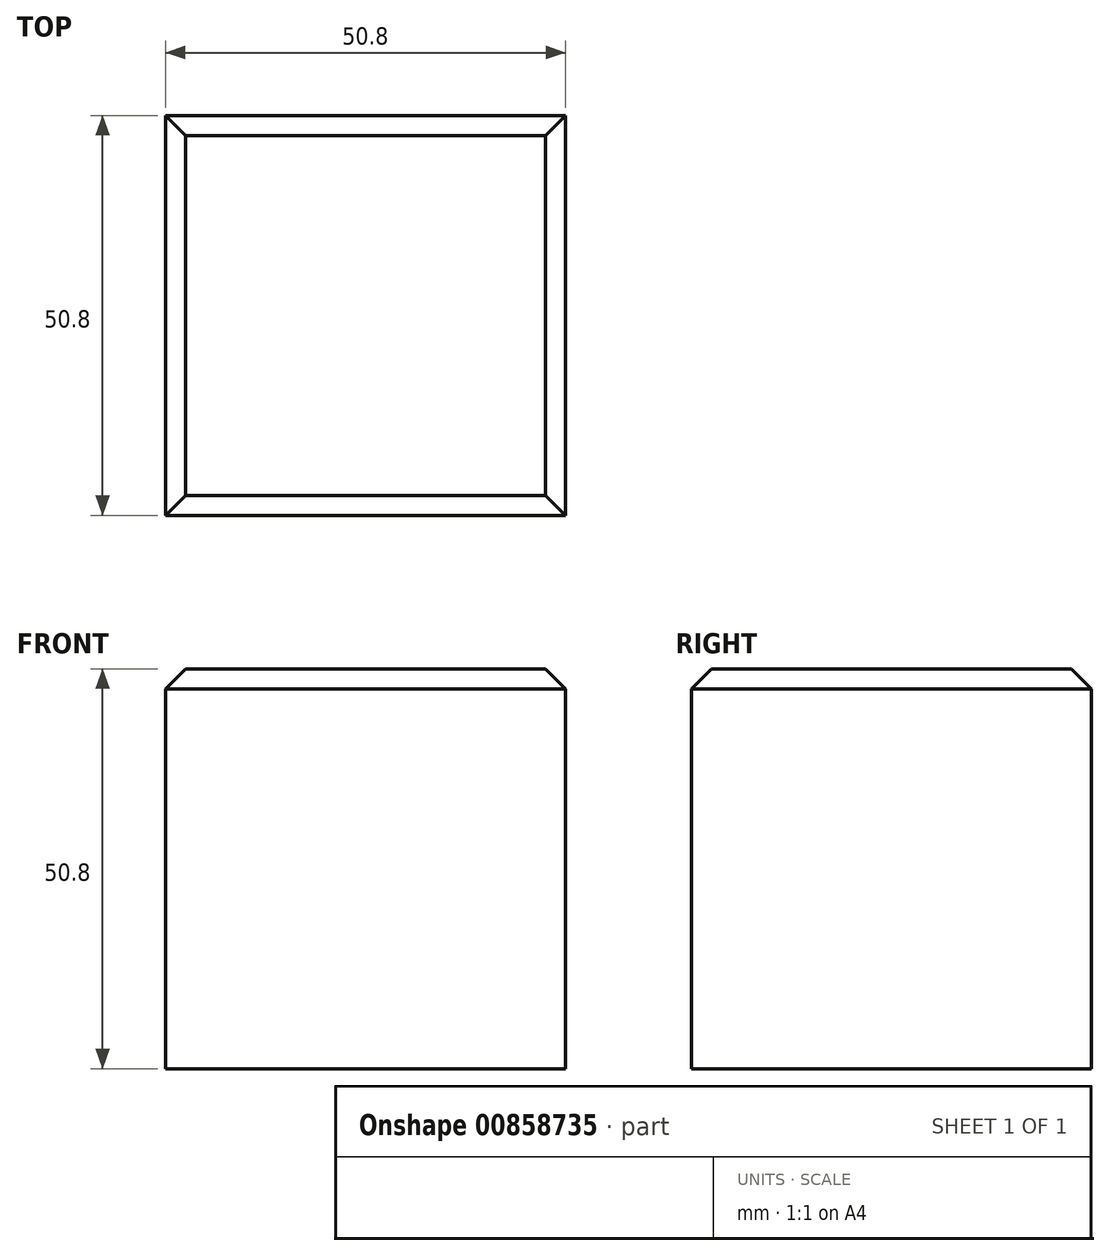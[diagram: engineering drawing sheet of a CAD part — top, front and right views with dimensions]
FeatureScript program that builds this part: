
annotation { "Feature Type Name" : "Feature", "Feature Type Description" : "" }
export const myFeature = defineFeature(function(context is Context, id is Id, definition is map)
    precondition{}
    {
        {
            var Q0;
            Q0=qCreatedBy(makeId("Top.planeOp"),FACE);
            var sketch = newSketch(context, id + "F0", { "sketchPlane" : qUnion([Q0])});
            skLineSegment(sketch, "E0.bottom", {"start": v(-25.4, 25.4) * mm, "end": v(25.4, 25.4) * mm});
            skLineSegment(sketch, "E0.top", {"start": v(-25.4, -25.4) * mm, "end": v(25.4, -25.4) * mm});
            skLineSegment(sketch, "E0.left", {"start": v(-25.4, 25.4) * mm, "end": v(-25.4, -25.4) * mm});
            skLineSegment(sketch, "E0.right", {"start": v(25.4, 25.4) * mm, "end": v(25.4, -25.4) * mm});
            skPoint(sketch, "E0.middle", {"position": v(0, 0) * mm});
            skSolve(sketch);
        }
        {
            var Q0;
            Q0 = qSketchRegion(id + "F0", true);
            extrude(context, id + "F1", {"entities" : qUnion([Q0]), "endBound" : BoundingType.SYMMETRIC, "depth" : 50.8 * mm, "offsetDistance" : 25.4 * mm});
        }
        {
            var Q0;
            Q0=makeQuery(id+"F1.opExtrude","CAP_FACE",FACE,{"disambiguationData":[OSD([sQuery(id+"F0.wireOp",EDGE,"E0.bottom"),sQuery(id+"F0.wireOp",EDGE,"E0.top"),sQuery(id+"F0.wireOp",EDGE,"E0.left"),sQuery(id+"F0.wireOp",EDGE,"E0.right")])],"isStart":false});
            chamfer(context, id + "F2", {"entities" : qUnion([Q0]), "width" : 2.54 * mm, "tangentPropagation" : true});
        }
    });
